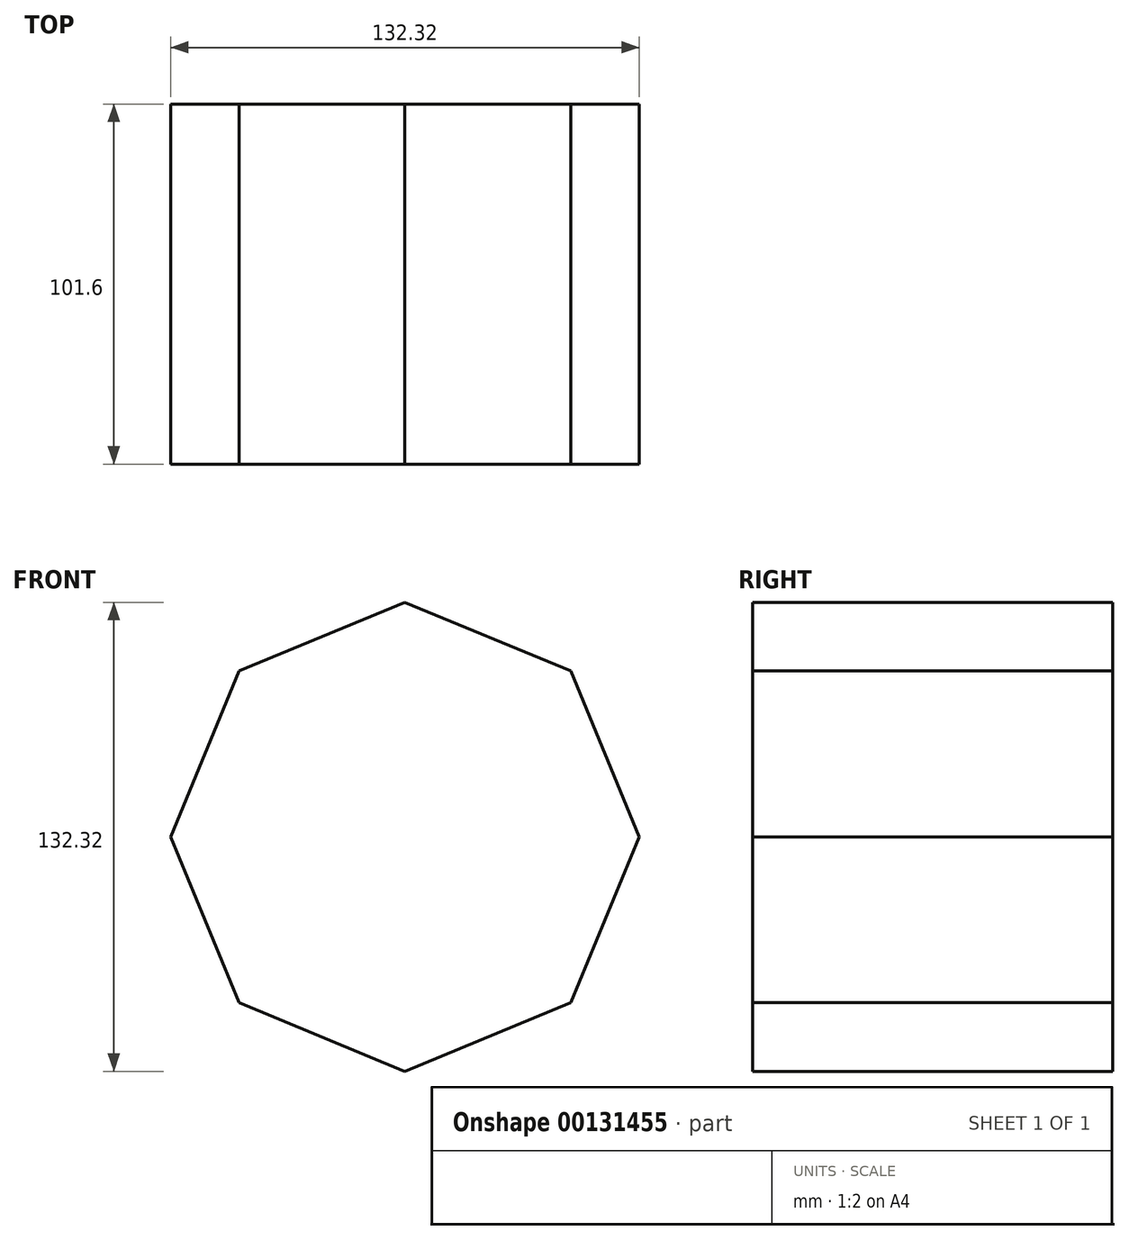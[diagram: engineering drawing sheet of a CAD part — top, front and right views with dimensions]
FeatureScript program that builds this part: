
annotation { "Feature Type Name" : "Feature", "Feature Type Description" : "" }
export const myFeature = defineFeature(function(context is Context, id is Id, definition is map)
    precondition{}
    {
        {
            var Q0;
            Q0=qCreatedBy(makeId("Front.planeOp"),FACE);
            var sketch = newSketch(context, id + "F0", { "sketchPlane" : qUnion([Q0])});
            skCircle(sketch, "E0.cCircle", {"center": v(0, 0) * mm, "radius": 66.16 * mm, "construction": true});
            skLineSegment(sketch, "E0.0", {"start": v(-66.16, 0) * mm, "end": v(-46.79, 46.79) * mm});
            skLineSegment(sketch, "E0.1", {"start": v(-46.79, 46.79) * mm, "end": v(0, 66.16) * mm});
            skLineSegment(sketch, "E0.2", {"start": v(0, 66.16) * mm, "end": v(46.79, 46.79) * mm});
            skLineSegment(sketch, "E0.3", {"start": v(46.79, 46.79) * mm, "end": v(66.16, 0) * mm});
            skLineSegment(sketch, "E0.4", {"start": v(66.16, 0) * mm, "end": v(46.79, -46.79) * mm});
            skLineSegment(sketch, "E0.5", {"start": v(46.79, -46.79) * mm, "end": v(0, -66.16) * mm});
            skLineSegment(sketch, "E0.6", {"start": v(0, -66.16) * mm, "end": v(-46.79, -46.79) * mm});
            skLineSegment(sketch, "E0.7", {"start": v(-46.79, -46.79) * mm, "end": v(-66.16, 0) * mm});
            skSolve(sketch);
        }
        {
            var Q0;
            Q0=makeQuery(id+"F0.imprint","IMPRINT",FACE,{"disambiguationData":[TD([[makeQuery(id+"F0.imprint","IMPRINT",EDGE,{"derivedFrom":sQuery(id+"F0.wireOp",EDGE,"E0.0")}),-1.0]])]});
            extrude(context, id + "F1", {"entities" : qUnion([Q0]), "depth" : 101.6 * mm});
        }
    });
